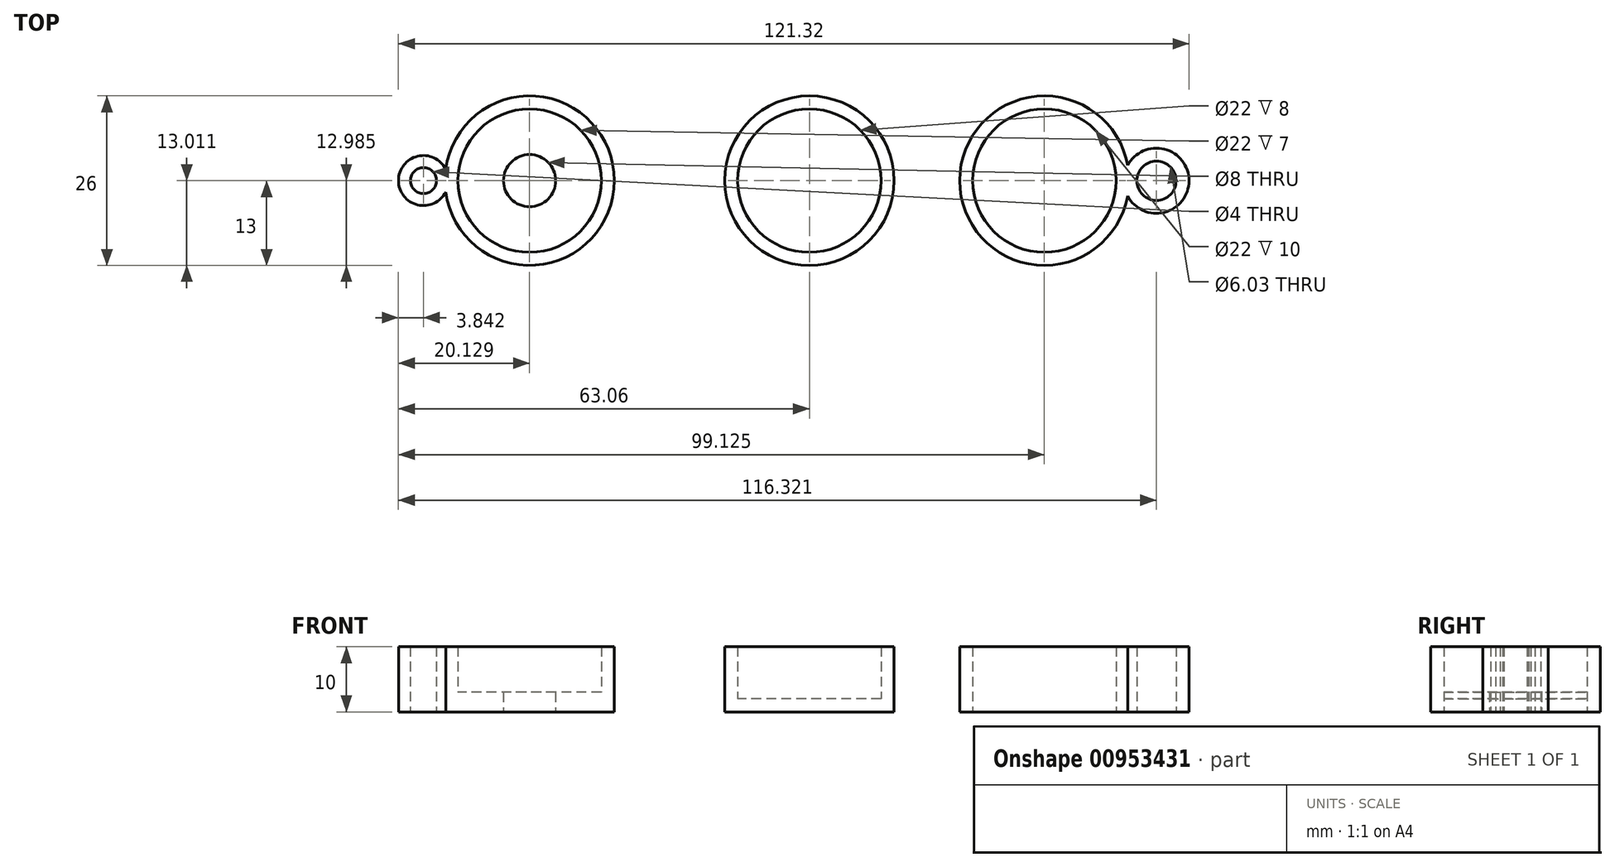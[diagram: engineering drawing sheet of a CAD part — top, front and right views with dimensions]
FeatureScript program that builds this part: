
annotation { "Feature Type Name" : "Feature", "Feature Type Description" : "" }
export const myFeature = defineFeature(function(context is Context, id is Id, definition is map)
    precondition{}
    {
        {
            var Q0;
            Q0=qCreatedBy(makeId("Top.planeOp"),FACE);
            var sketch = newSketch(context, id + "F0", { "sketchPlane" : qUnion([Q0])});
            skCircle(sketch, "E0", {"center": v(-42.93, 0) * mm, "radius": 13 * mm});
            skCircle(sketch, "E1", {"center": v(-42.93, 0) * mm, "radius": 11 * mm});
            skCircle(sketch, "E2", {"center": v(-42.93, 0) * mm, "radius": 4 * mm});
            skArc(sketch, "E3", {"start": v(-55.8, 1.78) * mm, "mid": v(-63.06, 0.01) * mm, "end": v(-55.81, -1.76) * mm});
            skCircle(sketch, "E4", {"center": v(-59.22, 0.01) * mm, "radius": 2 * mm});
            skSolve(sketch);
        }
        {
            var Q0;
            Q0=makeQuery(id+"F0.imprint","IMPRINT",FACE,{"disambiguationData":[TD([[makeQuery(id+"F0.imprint","IMPRINT",EDGE,{"derivedFrom":sQuery(id+"F0.wireOp",EDGE,"E0")}),1.0]])]});
            extrude(context, id + "F1", {"entities" : qUnion([Q0]), "depth" : 10 * mm, "offsetDistance" : 25 * mm});
        }
        {
            var Q0;
            Q0=makeQuery(id+"F0.imprint","IMPRINT",FACE,{"disambiguationData":[TD([[makeQuery(id+"F0.imprint","IMPRINT",EDGE,{"derivedFrom":sQuery(id+"F0.wireOp",EDGE,"E1")}),1.0]])]});
            extrude(context, id + "F2", {"entities" : qUnion([Q0]), "operationType" : NewBodyOperationType.ADD, "depth" : 3 * mm, "offsetDistance" : 25 * mm});
        }
        {
            var Q0;
            {var subQ0=sQuery(id+"F0.wireOp",EDGE,"E3");Q0=makeQuery(id+"F0.imprint","IMPRINT",FACE,{"disambiguationData":[TD([[makeQuery(id+"F0.imprint","IMPRINT",EDGE,{"derivedFrom":subQ0}),1.0]])]});}
            extrude(context, id + "F3", {"entities" : qUnion([Q0]), "operationType" : NewBodyOperationType.ADD, "depth" : 10 * mm, "offsetDistance" : 25 * mm});
        }
        {
            var Q0;
            Q0=qCreatedBy(makeId("Top.planeOp"),FACE);
            var sketch = newSketch(context, id + "F4", { "sketchPlane" : qUnion([Q0])});
            skCircle(sketch, "E5", {"center": v(0, 0) * mm, "radius": 13 * mm});
            skCircle(sketch, "E6", {"center": v(0, 0) * mm, "radius": 11 * mm});
            skSolve(sketch);
        }
        {
            var Q0;
            Q0=makeQuery(id+"F4.imprint","IMPRINT",FACE,{"disambiguationData":[TD([[makeQuery(id+"F4.imprint","IMPRINT",EDGE,{"derivedFrom":sQuery(id+"F4.wireOp",EDGE,"E5")}),1.0]])]});
            extrude(context, id + "F5", {"entities" : qUnion([Q0]), "depth" : 10 * mm, "offsetDistance" : 25 * mm});
        }
        {
            var Q0;
            Q0=makeQuery(id+"F4.imprint","IMPRINT",FACE,{"disambiguationData":[TD([[makeQuery(id+"F4.imprint","IMPRINT",EDGE,{"derivedFrom":sQuery(id+"F4.wireOp",EDGE,"E6")}),1.0]])]});
            extrude(context, id + "F6", {"entities" : qUnion([Q0]), "operationType" : NewBodyOperationType.ADD, "depth" : 2 * mm, "offsetDistance" : 25 * mm});
        }
        {
            var Q0;
            Q0=qCreatedBy(makeId("Top.planeOp"),FACE);
            var sketch = newSketch(context, id + "F7", { "sketchPlane" : qUnion([Q0])});
            skCircle(sketch, "E7", {"center": v(36.06, 0) * mm, "radius": 11 * mm});
            skCircle(sketch, "E8", {"center": v(36.06, 0) * mm, "radius": 13 * mm});
            skArc(sketch, "E9", {"start": v(48.85, -2.37) * mm, "mid": v(58.26, -0.02) * mm, "end": v(48.85, 2.34) * mm});
            skCircle(sketch, "E10", {"center": v(53.26, -0.01) * mm, "radius": 3.01 * mm});
            skSolve(sketch);
        }
        {
            var Q0;
            Q0=makeQuery(id+"F7.imprint","IMPRINT",FACE,{"disambiguationData":[TD([[makeQuery(id+"F7.imprint","IMPRINT",EDGE,{"derivedFrom":sQuery(id+"F7.wireOp",EDGE,"E7")}),-1.0]])]});
            var Q1;
            {var subQ0=sQuery(id+"F7.wireOp",EDGE,"E9");Q1=makeQuery(id+"F7.imprint","IMPRINT",FACE,{"disambiguationData":[TD([[makeQuery(id+"F7.imprint","IMPRINT",EDGE,{"derivedFrom":subQ0}),1.0]])]});}
            extrude(context, id + "F8", {"entities" : qUnion([Q0, Q1]), "depth" : 10 * mm, "offsetDistance" : 25 * mm});
        }
    });
